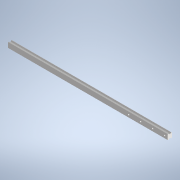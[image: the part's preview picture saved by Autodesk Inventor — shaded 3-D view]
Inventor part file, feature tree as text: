
AUTODESK INVENTOR PART (.ipt)
format: ipt  version: 2022 (Build 260153000, 153)  size: 162,816 bytes
history: native  units: mm (DEFAULTED — no unit token found)
features: other x21, sketch x2, extrude x1, hole x1, pattern_linear x1
ambient origin geometry x8: Origin, YZ Plane, XZ Plane, XY Plane, X Axis, Y Axis, Z Axis, Center Point
bodies: Solid1 (feature_tree)
feature tree (26):
  extrude  "Extrusion1"  Depth=10.0mm TaperAngle=0.0deg
  hole  "Hole1"  [1 undecoded]
  pattern_linear  "Rectangular Pattern1"  [2 undecoded]
  other  "4dummy_XY"
  other  "4dummy_YZ"
  other  "4dummy_ZX"
  other  "4dummy_X"
  other  "4dummy_Y"
  other  "4dummy_Z"
  other  "4dummy_Center"
  other  "4slide_XY"
  other  "4slide_YZ"
  other  "4slide_ZX"
  other  "4slide_X"
  other  "4slide_Y"
  other  "4slide_Z"
  other  "4slide_Center"
  other  "4track_XY"
  other  "4track_YZ"
  other  "4track_ZX"
  other  "4track_X"
  other  "4track_Y"
  other  "4track_Z"
  other  "4track_Center"
  sketch  "Sketch_18"  dims[d2=9.0mm d3=6.0mm d4=14.0mm d5=12.0mm d6=90.0deg d7=29.0mm d8=0.0mm d9=40.0mm d11=80.0mm d12=10.0mm d14=0.0mm d15=0.0mm]
  sketch  "Sketch2"  dims[d0=1676.4mm d1=0.0mm]
note: 3 required parameter values undecoded (feature->parameter linkage not recoverable at this tier; creation-order binding heuristic only, values carry confidence <= 0.55)
